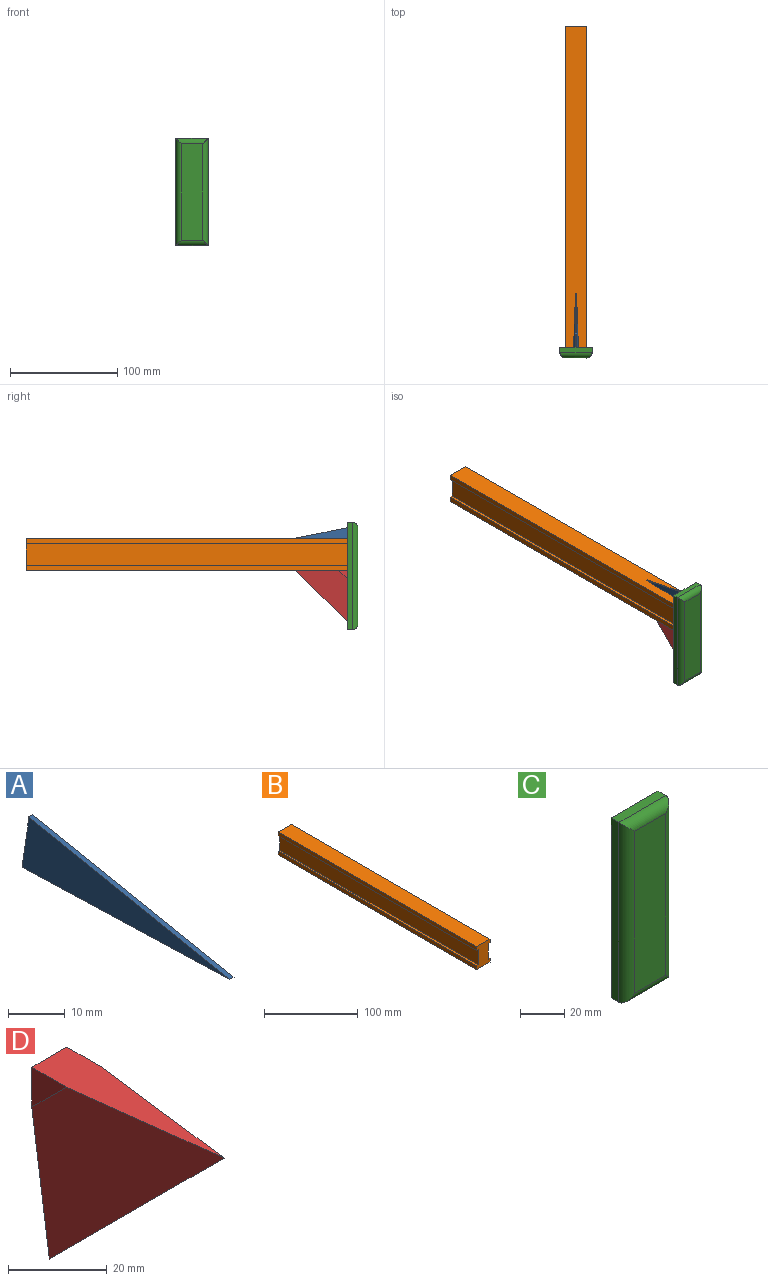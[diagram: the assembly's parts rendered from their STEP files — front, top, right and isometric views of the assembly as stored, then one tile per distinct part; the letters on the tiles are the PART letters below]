
ASSEMBLY  parts=4 mates=3
PART A: 5 faces, bbox 4.5x50x10 mm
  f0: plane 50x4.46mm, normal (0,0,-1), area 136.5mm2, adj f1,f2,f3,f4
  f1: plane 10x4.46mm, normal (0,1,0), area 27.3mm2, adj f0,f2,f3,f4
  f2: plane 50x10mm, normal (0,-0.2,0.98), area 51mm2, adj f0,f1,f3,f4
  f3: plane 50x10mm, normal (0.98,-0.03,0.17), area 253.9mm2, adj f0,f1,f2
  f4: plane 50x10mm, normal (-0.98,-0.03,0.17), area 253.9mm2, adj f0,f1,f2
PART B: 14 faces, bbox 20x300x30 mm
  f0: plane 300x20mm, normal (0,0,1), area 6000mm2, adj f1,f11,f12,f13
  f1: plane 300x5mm, normal (-1,0,0), area 1500mm2, adj f0,f2,f12,f13
  f2: plane 300x2.5mm, normal (0,0,-1), area 750mm2, adj f1,f3,f12,f13
  f3: plane 300x20mm, normal (-1,0,0), area 6000mm2, adj f2,f4,f12,f13
  f4: plane 300x2.5mm, normal (0,0,1), area 750mm2, adj f3,f5,f12,f13
  f5: plane 300x5mm, normal (-1,0,0), area 1500mm2, adj f4,f6,f12,f13
  f6: plane 300x20mm, normal (0,0,-1), area 6000mm2, adj f5,f7,f12,f13
  f7: plane 300x5mm, normal (1,0,0), area 1500mm2, adj f6,f8,f12,f13
  f8: plane 300x2.5mm, normal (0,0,1), area 750mm2, adj f7,f9,f12,f13
  f9: plane 300x20mm, normal (1,0,0), area 6000mm2, adj f8,f10,f12,f13
  f10: plane 300x2.5mm, normal (0,0,-1), area 750mm2, adj f9,f11,f12,f13
  f11: plane 300x5mm, normal (1,0,0), area 1500mm2, adj f0,f10,f12,f13
  f12: plane 30x20mm, normal (0,-1,0), area 500mm2, adj f0,f1,f2,f3,f4,f5,f6,f7
  f13: plane 30x20mm, normal (0,1,0), area 500mm2, adj f0,f1,f2,f3,f4,f5,f6,f7
PART C: 10 faces, bbox 30x10x100 mm
  f0: plane 30x5mm, normal (0,0,1), area 150mm2, adj f1,f3,f5,f6
  f1: plane 100x5mm, normal (-1,0,0), area 500mm2, adj f0,f2,f5,f7
  f2: plane 30x5mm, normal (0,0,-1), area 150mm2, adj f1,f3,f5,f9
  f3: plane 100x5mm, normal (1,0,0), area 500mm2, adj f0,f2,f5,f8
  f4: plane 90x20mm, normal (0,-1,0), area 1800mm2, adj f6,f7,f8,f9
  f5: plane 100x30mm, normal (0,1,0), area 3000mm2, adj f0,f1,f2,f3
  f6: cylinder r=5mm len=30mm, axis (1,0,0), area 207.1mm2, adj f0,f4,f7,f8
  f7: cylinder r=5mm len=100mm, axis (0,0,1), area 756.9mm2, adj f1,f4,f6,f9
  f8: cylinder r=5mm len=100mm, axis (0,0,-1), area 756.9mm2, adj f3,f4,f6,f9
  f9: cylinder r=5mm len=30mm, axis (-1,0,0), area 207.1mm2, adj f2,f4,f7,f8
PART D: 6 faces, bbox 10x50x50 mm
  f0: plane 50x10mm, normal (0,0,1), area 299.5mm2, adj f1,f2,f3,f4,f5
  f1: plane 50x10mm, normal (0,1,0), area 299.5mm2, adj f0,f2,f3,f4,f5
  f2: plane 9.9x9.9mm, normal (1,0,0), area 49mm2, adj f0,f1,f5
  f3: plane 9.9x9.9mm, normal (-1,0,0), area 49mm2, adj f0,f1,f4
  f4: plane 50x50mm, normal (-0.98,-0.12,-0.12), area 1219.5mm2, adj f0,f1,f3,f5
  f5: plane 50x50mm, normal (0.98,-0.12,-0.12), area 1219.5mm2, adj f0,f1,f2,f4
PLACE A rot(axis=(0,0,1),180deg) t=(14.38,-134.3,52.45)mm
PLACE B t=(10.05,145.77,-12.29)mm
PLACE C rot(axis=(0.73,0.68,0),0deg) t=(5.25,-154.23,-64.96)mm
PLACE D rot(axis=(0,0,1),180deg) t=(14.38,-124.57,-45.74)mm
MATE fastened D.f1 <-> C.f5  axis (0,-1,0) through (9.38,-154.23,-32.29)mm
MATE fastened B.f12 <-> C.f5  axis (0,-1,0) through (9.38,-154.23,-2.29)mm
MATE fastened C.f5 <-> A.f1  axis (0,1,0) through (9.38,-154.23,27.71)mm
